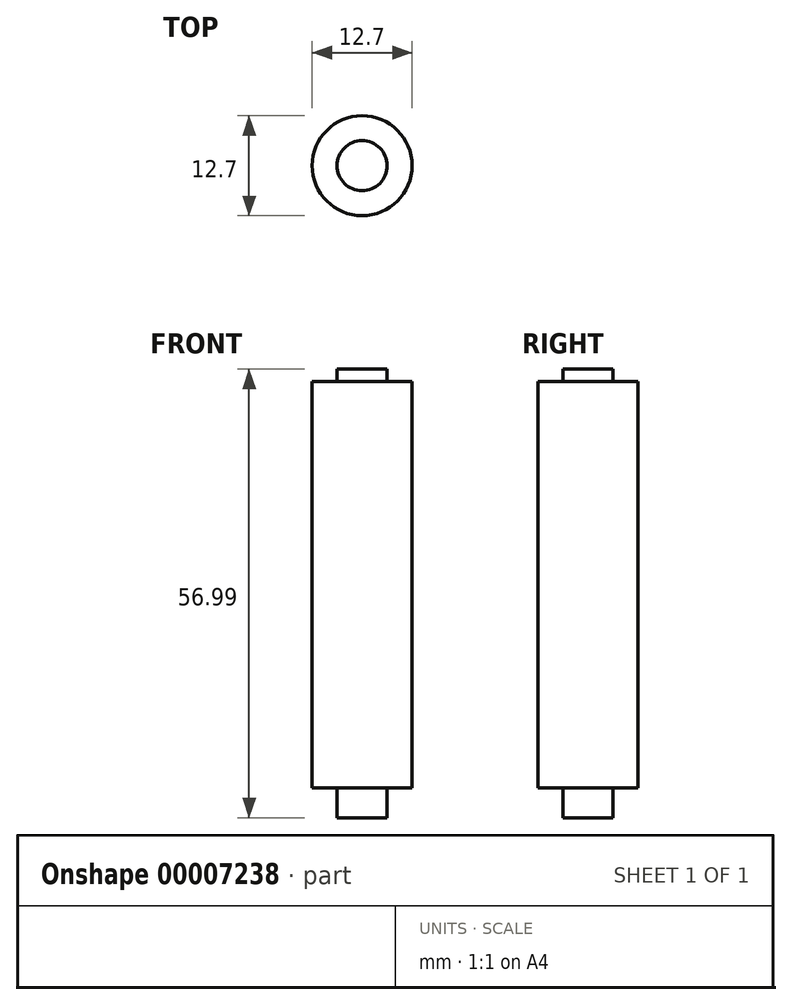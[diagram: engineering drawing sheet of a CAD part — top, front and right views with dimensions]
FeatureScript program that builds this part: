
annotation { "Feature Type Name" : "Feature", "Feature Type Description" : "" }
export const myFeature = defineFeature(function(context is Context, id is Id, definition is map)
    precondition{}
    {
        {
            var Q0;
            Q0=qCreatedBy(makeId("Top.planeOp"),FACE);
            var sketch = newSketch(context, id + "F0", { "sketchPlane" : qUnion([Q0])});
            skCircle(sketch, "E0", {"center": v(0, 0) * mm, "radius": 6.35 * mm});
            skSolve(sketch);
        }
        {
            var Q0;
            Q0=qSketchRegion(id+"F0",true);
            extrude(context, id + "F1", {"entities" : qUnion([Q0]), "depth" : 51.6 * mm});
        }
        {
            var Q0;
            Q0=makeQuery(id+"F1.opExtrude","CAP_FACE",FACE,{"disambiguationData":[OSD([sQuery(id+"F0.wireOp",EDGE,"E0")])],"isStart":true});
            var sketch = newSketch(context, id + "F2", { "sketchPlane" : qUnion([Q0])});
            skCircle(sketch, "E1", {"center": v(0, 0) * mm, "radius": 3.17 * mm});
            skSolve(sketch);
        }
        {
            var Q0;
            Q0=qSketchRegion(id+"F2",true);
            extrude(context, id + "F3", {"entities" : qUnion([Q0]), "operationType" : NewBodyOperationType.ADD, "depth" : 3.8 * mm});
        }
        {
            var Q0;
            Q0=makeQuery(id+"F1.opExtrude","CAP_FACE",FACE,{"disambiguationData":[OSD([sQuery(id+"F0.wireOp",EDGE,"E0")])],"isStart":false});
            var sketch = newSketch(context, id + "F4", { "sketchPlane" : qUnion([Q0])});
            skCircle(sketch, "E2", {"center": v(0, 0) * mm, "radius": 3.18 * mm});
            skSolve(sketch);
        }
        {
            var Q0;
            Q0=qSketchRegion(id+"F4",true);
            extrude(context, id + "F5", {"entities" : qUnion([Q0]), "operationType" : NewBodyOperationType.ADD, "depth" : 1.59 * mm});
        }
    });
